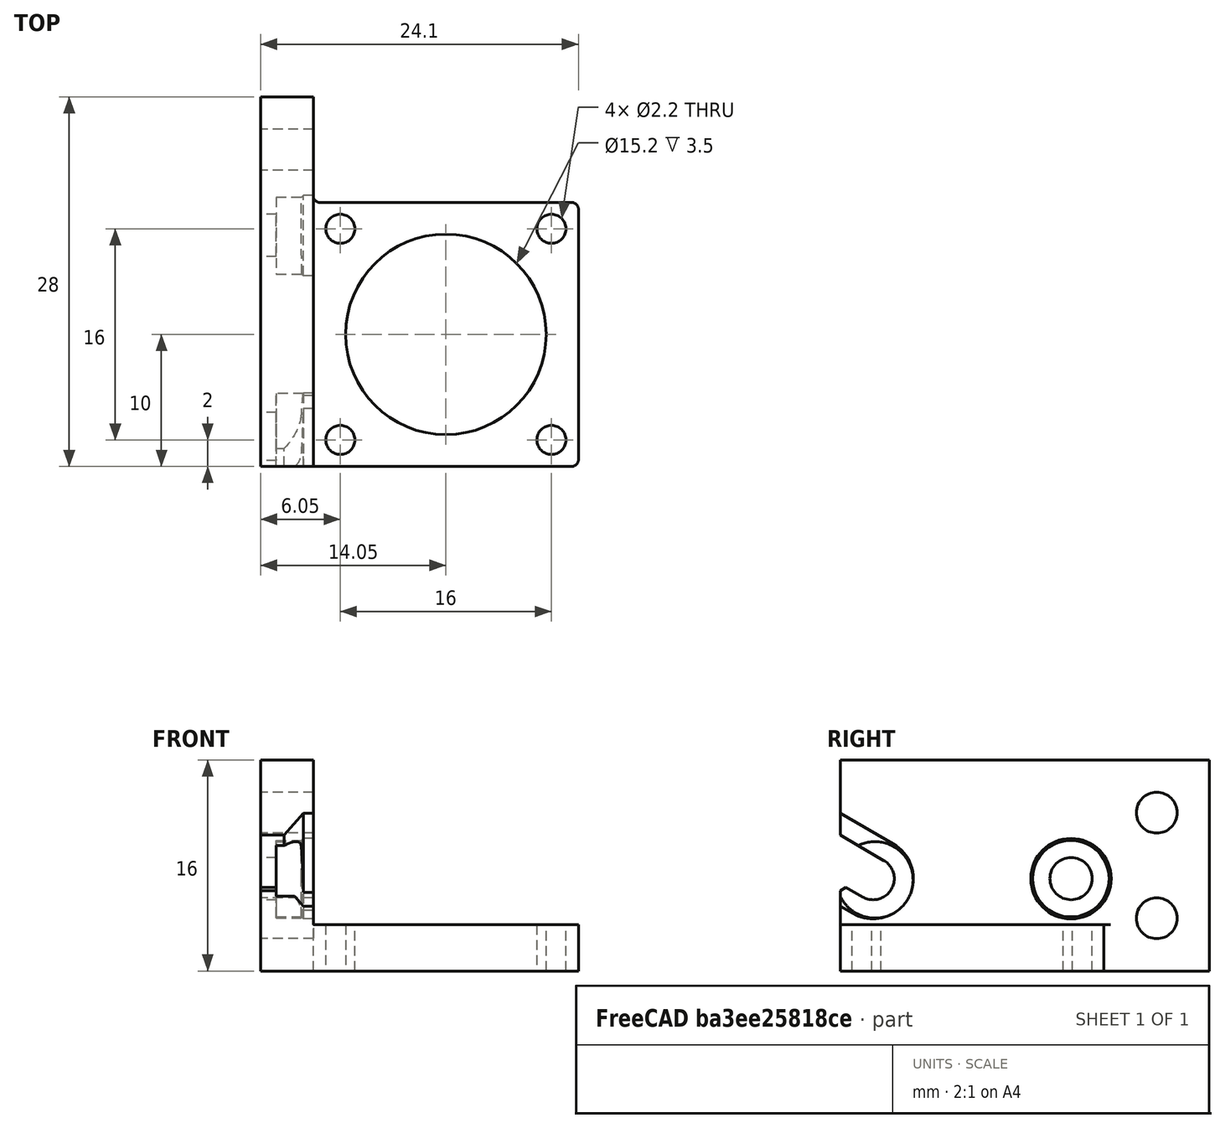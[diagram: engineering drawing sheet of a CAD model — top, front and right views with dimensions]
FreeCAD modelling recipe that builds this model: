
FCSTD DOCUMENT  (FreeCAD 0.18.4R)
Label: support_nema8_vis
License: All rights reserved
LicenseURL: http://en.wikipedia.org/wiki/All_rights_reserved
objects: Sketcher::SketchObject×2, Part::Feature×1, PartDesign::FeatureBase×1, PartDesign::Pocket×1, PartDesign::Body×1
note: 7 computed .brp shape members not serialized (recipe doc carries the construction recipe); baked Part::Feature solids carry a one-line shape summary decoded from their .brp

FEATURE [Part::Feature] Part__Feature  label="FusionComponent"
  shape: bbox 24.1 x 28 x 16 mm, 33 faces (baked)
FEATURE [PartDesign::FeatureBase] BaseFeature
  BaseFeature = -> Part__Feature
FEATURE [Sketcher::SketchObject] Sketch
  MapMode = 5
  Support = -> [XY_Plane]
FEATURE [Sketcher::SketchObject] Sketch001
  MapMode = 5
  Placement = pos=(5e-16,0,0) rot=(0.57735,0.57735,0.57735;2.0944rad)
  Support = -> [BaseFeature]
  sketch-geometry (2):
    g0: Circle CenterX=17.4848 CenterY=7.00133 CenterZ=0 NormalX=0 NormalY=0 NormalZ=1 AngleXU=0 Radius=2.9
    g1: Circle CenterX=2.62667 CenterY=6.9079 CenterZ=0 NormalX=0 NormalY=0 NormalZ=1 AngleXU=0 Radius=2.9
  constraints (2):
    c: Radius(g1) = 2.9
    c: Radius(g0) = 2.9
FEATURE [PartDesign::Pocket] Pocket
  BaseFeature = -> BaseFeature
  Length = 2.8
  Length2 = 100
  Profile = -> Sketch001
  Type = 0
FEATURE [PartDesign::Body] Body
  BaseFeature = -> Part__Feature
  Group = -> [BaseFeature,Sketch,Sketch001,Pocket]
  Origin = -> Origin
  Tip = -> Pocket
